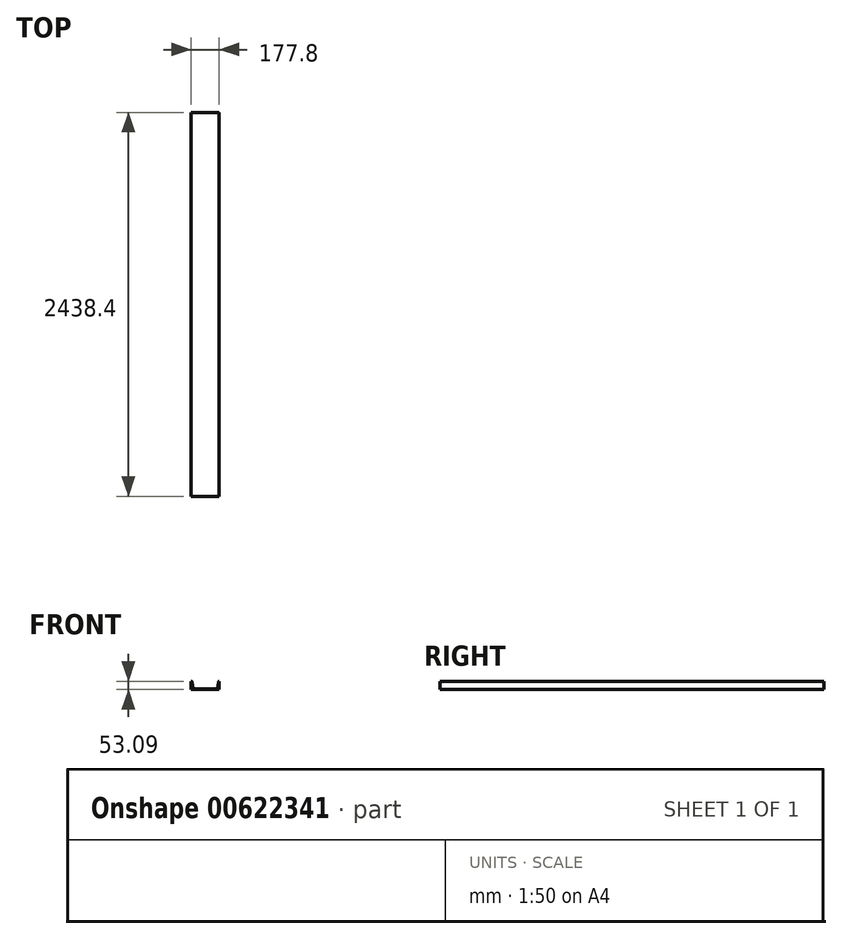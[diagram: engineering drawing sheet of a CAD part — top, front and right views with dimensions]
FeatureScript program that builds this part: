
annotation { "Feature Type Name" : "Feature", "Feature Type Description" : "" }
export const myFeature = defineFeature(function(context is Context, id is Id, definition is map)
    precondition{}
    {
        {
            var Q0;
            Q0=qCreatedBy(makeId("Front.planeOp"),FACE);
            var sketch = newSketch(context, id + "F0", { "sketchPlane" : qUnion([Q0])});
            skLineSegment(sketch, "E0", {"start": v(106.02, 0) * mm, "end": v(-71.78, 0) * mm});
            skLineSegment(sketch, "E1", {"start": v(-71.78, 0) * mm, "end": v(-71.78, 53.09) * mm});
            skLineSegment(sketch, "E2", {"start": v(-71.78, 53.09) * mm, "end": v(-69.24, 53.09) * mm});
            skLineSegment(sketch, "E3", {"start": v(-65.99, 50.32) * mm, "end": v(-59.65, 11.93) * mm});
            skLineSegment(sketch, "E4", {"start": v(-51.89, 5.33) * mm, "end": v(86.13, 5.33) * mm});
            skLineSegment(sketch, "E5", {"start": v(93.9, 11.93) * mm, "end": v(100.23, 50.32) * mm});
            skLineSegment(sketch, "E6", {"start": v(103.5, 53.09) * mm, "end": v(106.02, 53.09) * mm});
            skLineSegment(sketch, "E7", {"start": v(106.02, 53.09) * mm, "end": v(106.02, 0) * mm});
            skPoint(sketch, "E8.visualSharp", {"position": v(-66.44, 53.09) * mm});
            skArc(sketch, "E8.filletArc", {"start": v(-65.99, 50.32) * mm, "mid": v(-67.1, 52.3) * mm, "end": v(-69.24, 53.09) * mm});
            skPoint(sketch, "E9.visualSharp", {"position": v(100.7, 53.09) * mm});
            skArc(sketch, "E9.filletArc", {"start": v(103.5, 53.09) * mm, "mid": v(101.36, 52.3) * mm, "end": v(100.23, 50.32) * mm});
            skPoint(sketch, "E10.visualSharp", {"position": v(-58.57, 5.33) * mm});
            skArc(sketch, "E10.filletArc", {"start": v(-59.65, 11.93) * mm, "mid": v(-56.98, 7.2) * mm, "end": v(-51.89, 5.33) * mm});
            skPoint(sketch, "E11.visualSharp", {"position": v(92.82, 5.33) * mm});
            skArc(sketch, "E11.filletArc", {"start": v(86.13, 5.33) * mm, "mid": v(91.23, 7.2) * mm, "end": v(93.9, 11.93) * mm});
            skSolve(sketch);
        }
        {
            var Q0;
            Q0 = qSketchRegion(id + "F0", true);
            extrude(context, id + "F1", {"entities" : qUnion([Q0]), "depth" : 2438.4 * mm, "offsetDistance" : 30.48 * mm});
        }
    });
